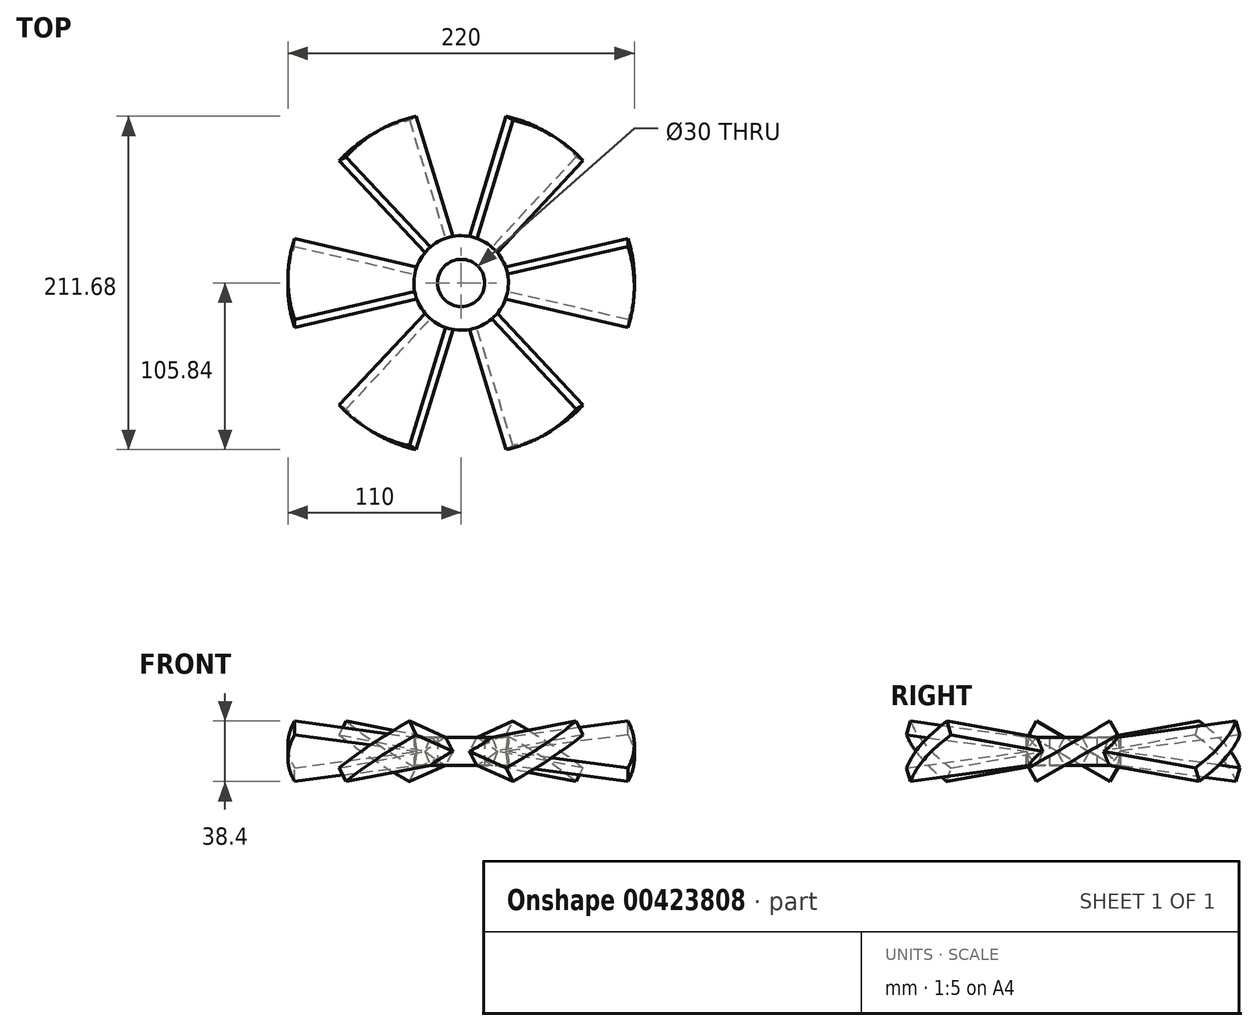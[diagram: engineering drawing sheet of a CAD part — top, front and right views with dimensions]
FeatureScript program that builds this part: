
annotation { "Feature Type Name" : "Feature", "Feature Type Description" : "" }
export const myFeature = defineFeature(function(context is Context, id is Id, definition is map)
    precondition{}
    {
        {
            var Q0;
            Q0=qCreatedBy(makeId("Right.planeOp"),FACE);
            var sketch = newSketch(context, id + "F0", { "sketchPlane" : qUnion([Q0])});
            skLineSegment(sketch, "E0", {"start": v(19.64, 11.34) * mm, "end": v(0, 0) * mm});
            skSolve(sketch);
        }
        {
            var Q0;
            Q0=sQuery(id+"F0.wireOp",EDGE,"E0");
            extrude(context, id + "F1", {"bodyType" : ToolBodyType.SURFACE, "surfaceEntities" : qUnion([Q0]), "oppositeDirection" : true, "depth" : 10.1 * mm});
        }
        {
            var Q0;
            Q0=makeQuery(id+"F1.opExtrude","SWEPT_FACE",FACE,{"disambiguationData":[OSD([sQuery(id+"F0.wireOp",EDGE,"E0")])]});
            var sketch = newSketch(context, id + "F2", { "sketchPlane" : qUnion([Q0])});
            skArc(sketch, "E1", {"start": v(105.9, -29.73) * mm, "mid": v(110, 0) * mm, "end": v(105.9, 29.73) * mm});
            skLineSegment(sketch, "E2", {"start": v(105.9, -29.73) * mm, "end": v(-5.05, 0) * mm});
            skLineSegment(sketch, "E3.MirrorCS", {"start": v(105.9, 29.73) * mm, "end": v(-5.05, 0) * mm});
            skSolve(sketch);
        }
        {
            var Q0;
            {var subQ5=sQuery(id+"F2.wireOp",EDGE,"E1");Q0=makeQuery(id+"F2.imprint","IMPRINT",FACE,{"disambiguationData":[TD([[makeQuery(id+"F2.imprint","IMPRINT",EDGE,{"derivedFrom":subQ5}),1.0]])]});}
            extrude(context, id + "F3", {"entities" : qUnion([Q0]), "depth" : 5 * mm, "hasSecondDirection" : true, "secondDirectionOppositeDirection" : true, "secondDirectionDepth" : 5 * mm});
        }
        {
            var Q0;
            Q0=qCreatedBy(makeId("Front.planeOp"),FACE);
            var sketch = newSketch(context, id + "F4", { "sketchPlane" : qUnion([Q0])});
            skLineSegment(sketch, "E4", {"start": v(0, 0) * mm, "end": v(0, 28.16) * mm});
            skSolve(sketch);
        }
        {
            var Q0;
            Q0=makeQuery(id+"F3.opExtrude","SWEPT_BODY",BODY,{"disambiguationData":[OSD([sQuery(id+"F0.wireOp",VERTEX,"E0.end"),sQuery(id+"F0.wireOp",EDGE,"E0"),sQuery(id+"F2.wireOp",EDGE,"E1"),sQuery(id+"F2.wireOp",EDGE,"E2"),sQuery(id+"F2.wireOp",EDGE,"E3.MirrorCS")])]});
            var Q1;
            Q1=sQuery(id+"F4.wireOp",EDGE,"E4");
            circularPattern(context, id + "F5", {"operationType" : NewBodyOperationType.ADD, "entities" : qUnion([Q0]), "axis" : qUnion([Q1]), "angle" : 360 * degree, "instanceCount" : 6, "equalSpace" : true});
        }
        {
            var Q0;
            Q0=qCreatedBy(makeId("Top.planeOp"),FACE);
            var sketch = newSketch(context, id + "F6", { "sketchPlane" : qUnion([Q0])});
            skCircle(sketch, "E5", {"center": v(0, 0) * mm, "radius": 30 * mm});
            skSolve(sketch);
        }
        {
            var Q0;
            Q0 = qSketchRegion(id + "F6", true);
            extrude(context, id + "F7", {"entities" : qUnion([Q0]), "operationType" : NewBodyOperationType.ADD, "depth" : 20 * mm, "hasSecondDirection" : true, "secondDirectionOppositeDirection" : true, "secondDirectionDepth" : 20 * mm});
        }
        {
            var Q0;
            Q0=qCreatedBy(makeId("Top.planeOp"),FACE);
            var Q1;
            {var subQ0=sQuery(id+"F2.wireOp",EDGE,"E2");Q1=makeQuery(id+"F7.boolean.opBoolean","INTERSECT",VERTEX,{"derivedFrom":[makeQuery(id+"F5.opPattern","COPY",FACE,{"derivedFrom":makeQuery(id+"F3.opExtrude","CAP_FACE",FACE,{"disambiguationData":[OSD([sQuery(id+"F0.wireOp",VERTEX,"E0.end"),sQuery(id+"F0.wireOp",EDGE,"E0"),sQuery(id+"F2.wireOp",EDGE,"E1"),subQ0,sQuery(id+"F2.wireOp",EDGE,"E3.MirrorCS")])],"isStart":true}),"instanceName":"4"}),makeQuery(id+"F5.opPattern","COPY",FACE,{"derivedFrom":makeQuery(id+"F3.opExtrude","SWEPT_FACE",FACE,{"disambiguationData":[OSD([subQ0])]}),"instanceName":"4"}),makeQuery(id+"F7.opExtrude","SWEPT_FACE",FACE,{"disambiguationData":[OSD([sQuery(id+"F6.wireOp",EDGE,"E5")])]})]});}
            cPlane(context, id + "F8", {"entities" : qUnion([Q0, Q1]), "cplaneType" : CPlaneType.PLANE_POINT, "offset" : 25 * mm, "width" : 150 * mm, "height" : 150 * mm});
        }
        {
            var Q0;
            Q0=qCreatedBy(id+"F8.planeOp",FACE);
            var sketch = newSketch(context, id + "F9", { "sketchPlane" : qUnion([Q0])});
            skCircle(sketch, "E6", {"center": v(0, 0) * mm, "radius": 30 * mm});
            skSolve(sketch);
        }
        {
            var Q0;
            Q0 = qSketchRegion(id + "F9", true);
            extrude(context, id + "F10", {"entities" : qUnion([Q0]), "operationType" : NewBodyOperationType.REMOVE, "depth" : 25 * mm});
        }
        {
            var Q0;
            Q0=qCreatedBy(makeId("Top.planeOp"),FACE);
            var Q1;
            {var subQ0=sQuery(id+"F2.wireOp",EDGE,"E3.MirrorCS");var subQ1=sQuery(id+"F2.wireOp",EDGE,"E2");var subQ2=sQuery(id+"F2.wireOp",EDGE,"E1");var subQ3=sQuery(id+"F0.wireOp",EDGE,"E0");var subQ4=sQuery(id+"F0.wireOp",VERTEX,"E0.end");var subQ5=makeQuery(id+"F3.opExtrude","CAP_FACE",FACE,{"disambiguationData":[OSD([subQ4,subQ3,subQ2,subQ1,subQ0])],"isStart":false});var subQ6=makeQuery(id+"F5.opPattern","COPY",FACE,{"derivedFrom":subQ5,"instanceName":"2"});var subQ7=makeQuery(id+"F3.opExtrude","SWEPT_FACE",FACE,{"disambiguationData":[OSD([subQ0])]});var subQ14=makeQuery(id+"F5.opPattern","COPY",FACE,{"derivedFrom":subQ7,"instanceName":"2"});Q1=makeQuery(id+"F7.boolean.opBoolean","INTERSECT",VERTEX,{"derivedFrom":[makeQuery(id+"F5.boolean.opBoolean","SPLIT",FACE,{"disambiguationData":[TD([subQ7])],"derivedFrom":subQ6}),makeQuery(id+"F5.boolean.opBoolean","SPLIT",FACE,{"disambiguationData":[TD([subQ7])],"derivedFrom":subQ14}),makeQuery(id+"F7.opExtrude","SWEPT_FACE",FACE,{"disambiguationData":[OSD([sQuery(id+"F6.wireOp",EDGE,"E5")])]})]});}
            cPlane(context, id + "F11", {"entities" : qUnion([Q0, Q1]), "cplaneType" : CPlaneType.PLANE_POINT, "offset" : 25 * mm, "width" : 150 * mm, "height" : 150 * mm});
        }
        {
            var Q0;
            Q0=qCreatedBy(id+"F11.planeOp",FACE);
            var sketch = newSketch(context, id + "F12", { "sketchPlane" : qUnion([Q0])});
            skCircle(sketch, "E7", {"center": v(0, 0) * mm, "radius": 30 * mm});
            skSolve(sketch);
        }
        {
            var Q0;
            Q0 = qSketchRegion(id + "F12", true);
            extrude(context, id + "F13", {"entities" : qUnion([Q0]), "operationType" : NewBodyOperationType.REMOVE, "oppositeDirection" : true, "depth" : 25 * mm});
        }
        {
            var Q0;
            Q0=makeQuery(id+"F13.boolean.opBoolean","COPY",FACE,{"derivedFrom":makeQuery(id+"F13.opExtrude","CAP_FACE",FACE,{"disambiguationData":[OSD([sQuery(id+"F12.wireOp",EDGE,"E7")])],"isStart":true})});
            var sketch = newSketch(context, id + "F14", { "sketchPlane" : qUnion([Q0])});
            skCircle(sketch, "E8", {"center": v(0, 0) * mm, "radius": 15 * mm});
            skSolve(sketch);
        }
        {
            var Q0;
            Q0=makeQuery(id+"F14.imprint","IMPRINT",FACE,{"disambiguationData":[TD([[makeQuery(id+"F14.imprint","IMPRINT",EDGE,{"derivedFrom":sQuery(id+"F14.wireOp",EDGE,"E8")}),1.0]])]});
            extrude(context, id + "F15", {"entities" : qUnion([Q0]), "operationType" : NewBodyOperationType.REMOVE, "oppositeDirection" : true, "depth" : 25 * mm});
        }
    });
